# Revit family: Plymold-Essentials-Quest_Metal_Chairhead-
name_source: partatom
category: Furniture
units: mm (PartAtom-declared; Revit-internal decimal feet)

## family parameters
Always vertical = Yes
Cut with Voids When Loaded = No
OmniClass Number = 23.40.20.00
OmniClass Title = General Furniture and Specialties
Render Appearance Source = Family Geometry
Room Calculation Point = No
Shared = No
Work Plane-Based = No

## types (1)
- 6710CS
    Assembly Code = E2020200
    BACK MATERIAL = PLY - Onyx Black Powdercoat
    Brand = Chairheads & Bolt-Down
    CAP MATERIAL = PLY - Plastic Black
    Cost = 0 $
    Default Elevation = 0"
    Depth = 17 1/2"
    Description = Quest Metal Chairhead with Composite Seat - 17 1/2”W x 17 1/2”D x 17”H
    FRAME MATERIAL = PLY - Onyx Black Powdercoat
    HARDWARE MATERIAL = PLY - Onyx Black Powdercoat
    Height = 17"
    Keynote = 12500
    Manufacturer = Plymold
    Model = 6710CS
    Product Documentation Link = https://plymold.com
    Revit Model Built By = https://www.servex-us.com
    SEAT MATERIAL = PLY - Plastic Blue
    Sustainability = https://plymold.com
    Type Comments = Swivels & Chairheads
    URL = https://plymold.com
    Width = 17 1/2"

## geometry (parser evidence)
native form markers: Sweep x5
no freeform markers — native parametric forms only
